# Revit family: 3-689-xx - IO Ceiling Mount
name_source: partatom
category: Luminarias
units: mm (PartAtom-declared; Revit-internal decimal feet)

## family parameters
Anfitrión = Techo
Compartido = No
Corte con vacíos al cargar = No
Cota de conector redondo = Diámetro de uso
Número OmniClass = 23.80.70.11
Origen de luz = Sí
Punto de cálculo de habitación = No
Siempre vertical = Sí
Tipo de pieza = Normal
Título OmniClass = Luminaries for Internal Lighting

## types (2) — shared parameters
Archivo de red fotométrica = 3-689 iO Ceiling Mount.ies
Cambio de temperatura de color de luz atenuada = <Ninguno>
Comentarios de vataje = 2 x 10.1 W at 120 V
Fabricante = Oxygen Lighting and Fans
Filtro de color = 16777215
Lámpara = LED Array
Main Diffuser = Matte White Acrylic
Metal Finish = 24 - Satin Nickel
Modelo = 3-689-xx / IO Ceiling Mount
References = Ref. 3 = 120 V / Ref. 37 = 277 V
URL = www.oxygenlighting.com
Voltage = 120 V
Voltage Input = 120 V or 277 V - 50/60 Hz
Ángulo de inclinación = 90.00°
zero-valued in all types: Elevación por defecto

## type names (no varying parameters)
- 3-689-24 / Satin Nickel - Matte White Acrylic
- 3-689-40 / Aged Brass - Matte White Acrylic

## geometry (parser evidence)
native form markers: Sweep x4
no freeform markers — native parametric forms only
